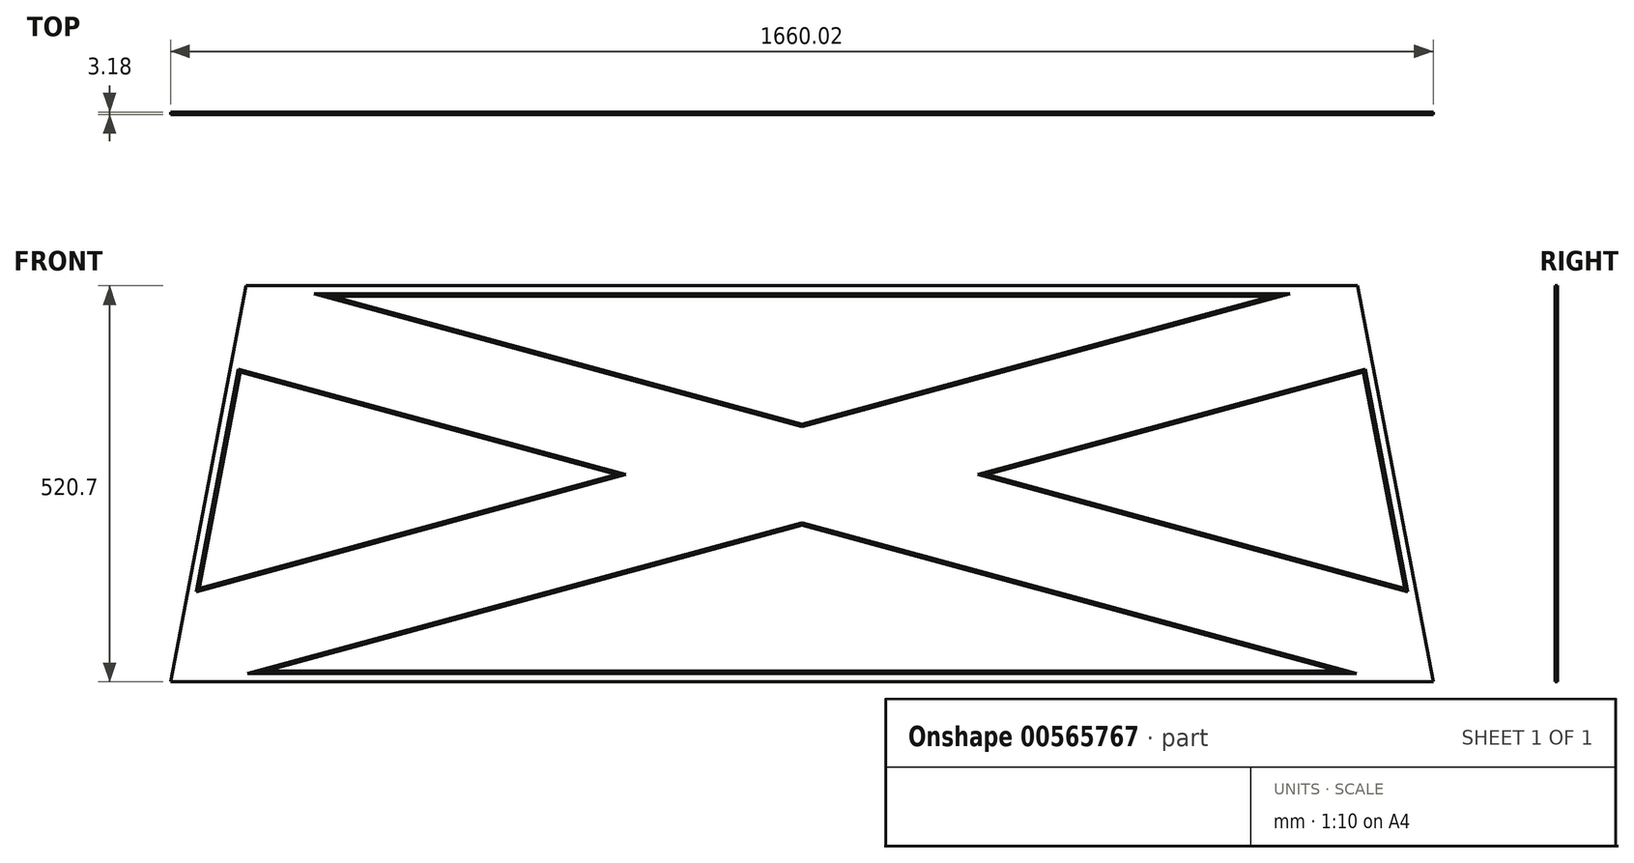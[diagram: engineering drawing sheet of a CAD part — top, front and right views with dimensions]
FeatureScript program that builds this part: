
annotation { "Feature Type Name" : "Feature", "Feature Type Description" : "" }
export const myFeature = defineFeature(function(context is Context, id is Id, definition is map)
    precondition{}
    {
        {
            var Q0;
            Q0=qCreatedBy(makeId("Front.planeOp"),FACE);
            var sketch = newSketch(context, id + "F0", { "sketchPlane" : qUnion([Q0])});
            skLineSegment(sketch, "E0", {"start": v(0, 0) * mm, "end": v(1660.02, 0) * mm});
            skLineSegment(sketch, "E1", {"start": v(1660.02, 0) * mm, "end": v(1560.64, 520.7) * mm});
            skLineSegment(sketch, "E2", {"start": v(1560.64, 520.7) * mm, "end": v(99.38, 520.7) * mm});
            skLineSegment(sketch, "E3", {"start": v(99.38, 520.7) * mm, "end": v(0, 0) * mm});
            skLineSegment(sketch, "E4", {"start": v(91.88, 406.93) * mm, "end": v(37.67, 122.89) * mm});
            skLineSegment(sketch, "E5", {"start": v(124.84, 13.97) * mm, "end": v(1535.18, 13.97) * mm});
            skLineSegment(sketch, "E6", {"start": v(212.53, 506.73) * mm, "end": v(1447.49, 506.73) * mm});
            skLineSegment(sketch, "E7", {"start": v(1622.34, 122.89) * mm, "end": v(1568.13, 406.93) * mm});
            skLineSegment(sketch, "E8", {"start": v(91.88, 406.93) * mm, "end": v(586.41, 272.29) * mm});
            skLineSegment(sketch, "E9", {"start": v(1622.34, 122.89) * mm, "end": v(1073.6, 272.29) * mm});
            skLineSegment(sketch, "E10", {"start": v(37.67, 122.89) * mm, "end": v(586.41, 272.29) * mm});
            skLineSegment(sketch, "E11", {"start": v(1568.13, 406.93) * mm, "end": v(1073.6, 272.29) * mm});
            skLineSegment(sketch, "E12.trimOffspring", {"start": v(830, 338.61) * mm, "end": v(1447.49, 506.73) * mm});
            skLineSegment(sketch, "E13.trimOffspring", {"start": v(830, 205.96) * mm, "end": v(1535.18, 13.97) * mm});
            skLineSegment(sketch, "E14.trimOffspring", {"start": v(830, 338.61) * mm, "end": v(212.53, 506.73) * mm});
            skLineSegment(sketch, "E15.trimOffspring", {"start": v(830, 205.96) * mm, "end": v(124.84, 13.97) * mm});
            skPoint(sketch, "E16.orphan", {"position": v(1643.13, 13.97) * mm});
            skPoint(sketch, "E17.orphan", {"position": v(1549.09, 506.73) * mm});
            skPoint(sketch, "E18.orphan", {"position": v(110.93, 506.73) * mm});
            skPoint(sketch, "E19.orphan", {"position": v(16.89, 13.97) * mm});
            skSolve(sketch);
        }
        {
            var Q0;
            Q0=makeQuery(id+"F0.imprint","IMPRINT",FACE,{"disambiguationData":[TD([[makeQuery(id+"F0.imprint","IMPRINT",EDGE,{"derivedFrom":sQuery(id+"F0.wireOp",EDGE,"E0")}),1.0]])]});
            extrude(context, id + "F1", {"entities" : qUnion([Q0]), "depth" : 3.17 * mm, "offsetDistance" : 25.4 * mm});
        }
        {
            var Q0;
            Q0=makeQuery(id+"F1.opExtrude","CAP_EDGE",EDGE,{"disambiguationData":[OSD([sQuery(id+"F0.wireOp",EDGE,"E4")])],"isStart":false});
            var Q1;
            Q1=makeQuery(id+"F1.opExtrude","CAP_EDGE",EDGE,{"disambiguationData":[OSD([sQuery(id+"F0.wireOp",EDGE,"E10")])],"isStart":false});
            var Q2;
            Q2=makeQuery(id+"F1.opExtrude","CAP_EDGE",EDGE,{"disambiguationData":[OSD([sQuery(id+"F0.wireOp",EDGE,"E8")])],"isStart":false});
            var Q3;
            Q3=makeQuery(id+"F1.opExtrude","CAP_EDGE",EDGE,{"disambiguationData":[OSD([sQuery(id+"F0.wireOp",EDGE,"E14.trimOffspring")])],"isStart":false});
            var Q4;
            Q4=makeQuery(id+"F1.opExtrude","CAP_EDGE",EDGE,{"disambiguationData":[OSD([sQuery(id+"F0.wireOp",EDGE,"E6")])],"isStart":false});
            var Q5;
            Q5=makeQuery(id+"F1.opExtrude","CAP_EDGE",EDGE,{"disambiguationData":[OSD([sQuery(id+"F0.wireOp",EDGE,"E12.trimOffspring")])],"isStart":false});
            var Q6;
            Q6=makeQuery(id+"F1.opExtrude","CAP_EDGE",EDGE,{"disambiguationData":[OSD([sQuery(id+"F0.wireOp",EDGE,"E11")])],"isStart":false});
            var Q7;
            Q7=makeQuery(id+"F1.opExtrude","CAP_EDGE",EDGE,{"disambiguationData":[OSD([sQuery(id+"F0.wireOp",EDGE,"E9")])],"isStart":false});
            var Q8;
            Q8=makeQuery(id+"F1.opExtrude","CAP_EDGE",EDGE,{"disambiguationData":[OSD([sQuery(id+"F0.wireOp",EDGE,"E7")])],"isStart":false});
            var Q9;
            Q9=makeQuery(id+"F1.opExtrude","CAP_EDGE",EDGE,{"disambiguationData":[OSD([sQuery(id+"F0.wireOp",EDGE,"E5")])],"isStart":false});
            var Q10;
            Q10=makeQuery(id+"F1.opExtrude","CAP_EDGE",EDGE,{"disambiguationData":[OSD([sQuery(id+"F0.wireOp",EDGE,"E13.trimOffspring")])],"isStart":false});
            var Q11;
            Q11=makeQuery(id+"F1.opExtrude","CAP_EDGE",EDGE,{"disambiguationData":[OSD([sQuery(id+"F0.wireOp",EDGE,"E15.trimOffspring")])],"isStart":false});
            chamfer(context, id + "F2", {"entities" : qUnion([Q0, Q1, Q2, Q3, Q4, Q5, Q6, Q7, Q8, Q9, Q10, Q11]), "width" : 3.17 * mm, "tangentPropagation" : true});
        }
    });
